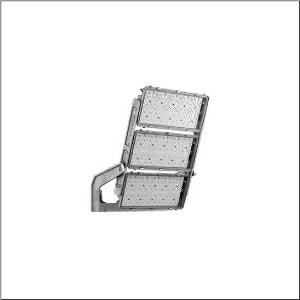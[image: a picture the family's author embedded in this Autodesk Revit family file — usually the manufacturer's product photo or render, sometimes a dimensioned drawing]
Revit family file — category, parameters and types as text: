
# Revit family: floodlight_fl_11_maxi_pro_remote___pl43_5xa779425a01aa_2185
name_source: partatom
category: Lighting Fixtures
units: mm (PartAtom-declared; Revit-internal decimal feet)

## family parameters
Cut with Voids When Loaded = No
Host = Face
Light Source = No
Part Type = Normal
Room Calculation Point = No
Round Connector Dimension = Use Diameter
Shared = No

## types (1)
- --- (1 x LED, 162210 lm, 1334.7 W, 3000K)
    Apparent Load = 1335 VA
    CIE Flux Codes = 25 74 99 100 100
    Color Rendering = 70
    Color Temperature = 3000K
    Default Elevation = 1800 mm
    Description = Floodlight FL 11  maxi  pro Remote floodlight; light control with lens of PMMA; cover panel of toughened safety glass, transparent; light distribution: PL43, asymmetric direct distribution, LEDcolour temperature: 3000K, colour rendering: CRI > 70, light colour: 730; brightness control: DALI 2 (1 DALI address); with terminal, 8-pole, max. 2.5mm², mains connection: 220..240V/380..400V AC, 50/60Hz, surge voltage resistance: line to ground: 10kV, ECG replaceable separately, LED unit replaceable without ESD environment, dustproof LED module, dimming range 10..100%, no afterglow with DALI off / DMX off command; floodlight with 2x LED unit of diecast aluminium, coated grey; length: 713mm / width: 651mm / height: 338mm; mounting bracket, of diecast aluminium, uncoated, natural, equipment: Power, protection rating (complete): IP66; insulation class (complete): insulation class I (protective earthing); certification: CE, ENEC, VDE; ball protection: ball impact resistance with accessories, rated ambient temperature 10°C, only for outdoor installations, permissible operating ambient temperature: -40..+30°C, permissible storage temperature: -40..+85°C; packaging unit: 1 piece

Light Distribution: PL43
    Height = 320 mm
    Lamp = 1 x LED
    Lamp Light Flux = 162210 lm
    Lamp Power = 1334.7 W
    Lamp count = 1
    Length = 1002 mm
    Luminous efficacy = 122 lm/W
    Manufacturer = Siteco
    ModVariant = No
    Model = 5XA779425A01AA
    Number of Poles = 1
    OnlyDefault = Yes
    Power Factor = 1
    Product Name = Floodlight FL 11 maxi pro Remote | PL43
    Product group = floodlight | pylon top
    ProductGroupID = 6101
    Protection Class = Protection class I
    Protection Degree = IP 66
    RLX_Detail_Level = 1
    RlxData = <blob elided: 52421 chars, md5=d994952f>
    Socket = socket
    Standby Power = 0 W
    System Light Flux = 162210 lm
    System Power = 1335 W
    Type Comments = factory setting: luminous flux: 100 % | dim-lin: 254 | 920 mA
    Type Image = l_1006784.jpg
    URL = http://relux.com
    VarID = @adj_005867
    Voltage = 0 V
    Weight = 0.00 kg
    Width = 655 mm

## geometry (parser evidence)
native form markers: Blend x4, Sweep x13
no freeform markers — native parametric forms only
